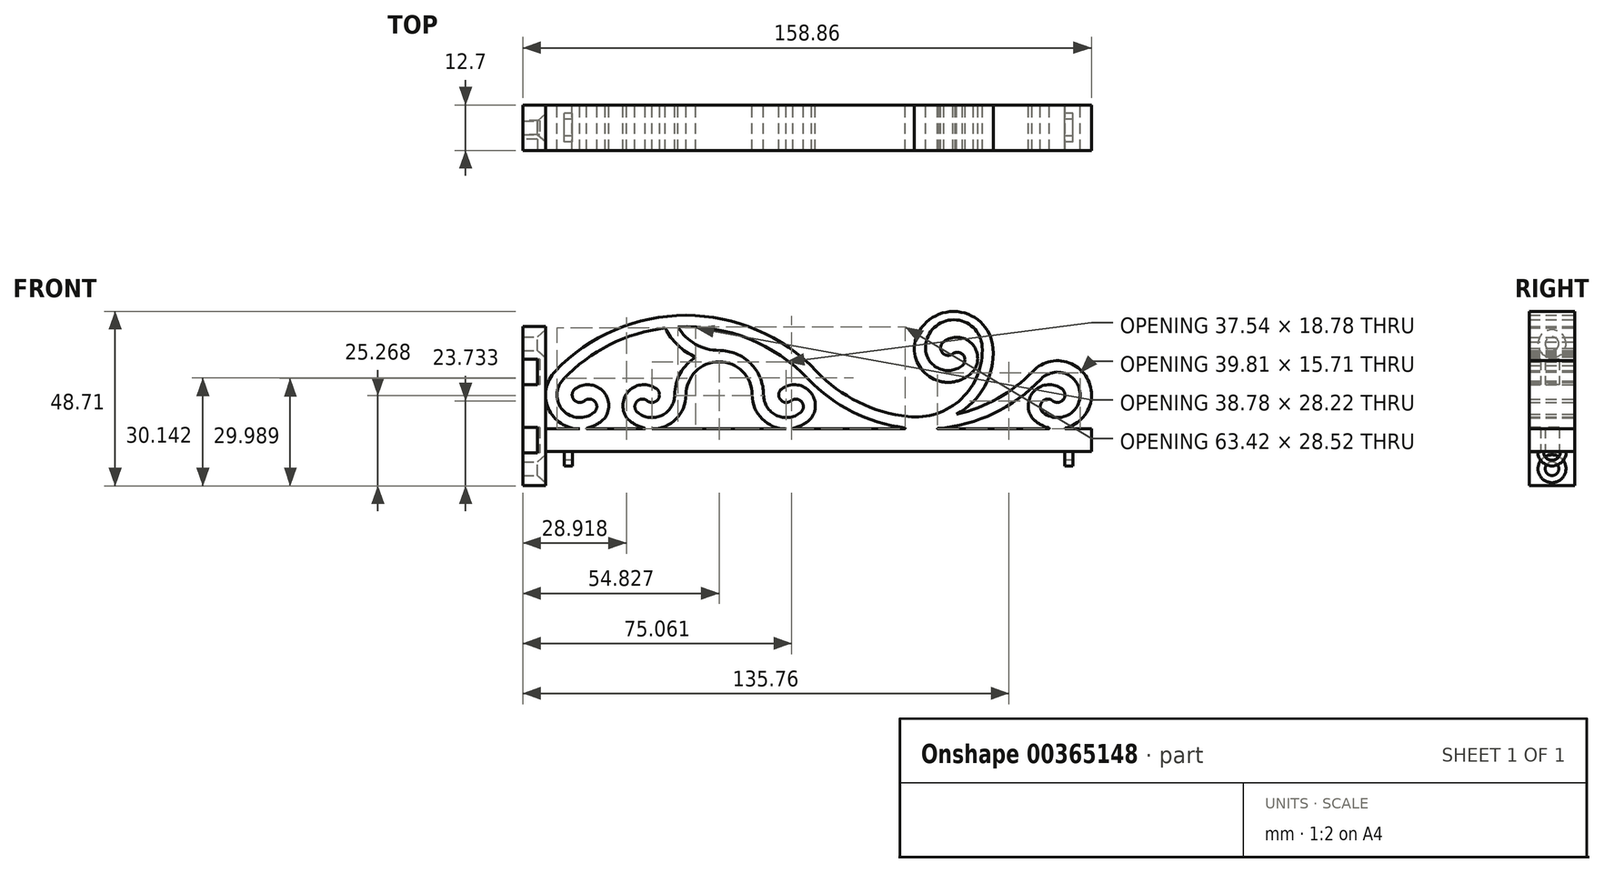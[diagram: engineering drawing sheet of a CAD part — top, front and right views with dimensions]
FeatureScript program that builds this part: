
annotation { "Feature Type Name" : "Feature", "Feature Type Description" : "" }
export const myFeature = defineFeature(function(context is Context, id is Id, definition is map)
    precondition{}
    {
        {
            var Q0;
            Q0=qCreatedBy(makeId("Front.planeOp"),FACE);
            var sketch = newSketch(context, id + "F0", { "sketchPlane" : qUnion([Q0])});
            skLineSegment(sketch, "E0.bottom", {"start": v(-3.17, 22.23) * mm, "end": v(3.18, 22.23) * mm, "construction": true});
            skLineSegment(sketch, "E0.top", {"start": v(-3.17, -22.23) * mm, "end": v(3.18, -22.23) * mm, "construction": true});
            skLineSegment(sketch, "E0.right", {"start": v(3.18, 22.23) * mm, "end": v(3.18, -22.23) * mm});
            skPoint(sketch, "E0.middle", {"position": v(0, 0) * mm});
            skLineSegment(sketch, "E1", {"start": v(3.18, 22.23) * mm, "end": v(-3.17, 22.23) * mm});
            skLineSegment(sketch, "E2", {"start": v(3.18, -22.23) * mm, "end": v(-3.17, -22.23) * mm});
            skLineSegment(sketch, "E3", {"start": v(-3.17, 22.23) * mm, "end": v(-3.17, -22.23) * mm});
            skSolve(sketch);
        }
        {
            var Q0;
            Q0=makeQuery(id+"F0.imprint","IMPRINT",FACE,{"disambiguationData":[TD([[makeQuery(id+"F0.imprint","IMPRINT",EDGE,{"derivedFrom":sQuery(id+"F0.wireOp",EDGE,"E0.right")}),-1.0]])]});
            extrude(context, id + "F1", {"entities" : qUnion([Q0]), "endBound" : BoundingType.SYMMETRIC, "depth" : 12.7 * mm});
        }
        {
            var Q0;
            Q0=makeQuery(id+"F1.opExtrude","SWEPT_FACE",FACE,{"disambiguationData":[OSD([sQuery(id+"F0.wireOp",EDGE,"E3")])]});
            var sketch = newSketch(context, id + "F2", { "sketchPlane" : qUnion([Q0])});
            skLineSegment(sketch, "E4", {"start": v(0, 9.53) * mm, "end": v(0, -9.53) * mm, "construction": true});
            skLineSegment(sketch, "E5.bottom", {"start": v(-1.97, 13.08) * mm, "end": v(1.97, 13.08) * mm});
            skLineSegment(sketch, "E5.top", {"start": v(-1.97, 5.97) * mm, "end": v(1.97, 5.97) * mm});
            skLineSegment(sketch, "E5.left", {"start": v(-1.97, 13.08) * mm, "end": v(-1.97, 5.97) * mm});
            skLineSegment(sketch, "E5.right", {"start": v(1.97, 13.08) * mm, "end": v(1.97, 5.97) * mm});
            skPoint(sketch, "E5.middle", {"position": v(0, 9.53) * mm});
            skLineSegment(sketch, "E6.bottom", {"start": v(-1.97, -5.97) * mm, "end": v(1.97, -5.97) * mm});
            skLineSegment(sketch, "E6.top", {"start": v(-1.97, -13.08) * mm, "end": v(1.97, -13.08) * mm});
            skLineSegment(sketch, "E6.left", {"start": v(-1.97, -5.97) * mm, "end": v(-1.97, -13.08) * mm});
            skLineSegment(sketch, "E6.right", {"start": v(1.97, -5.97) * mm, "end": v(1.97, -13.08) * mm});
            skPoint(sketch, "E6.middle", {"position": v(0, -9.53) * mm});
            skSolve(sketch);
        }
        {
            var Q0;
            Q0=makeQuery(id+"F2.imprint","IMPRINT",FACE,{"disambiguationData":[TD([[makeQuery(id+"F2.imprint","IMPRINT",EDGE,{"derivedFrom":sQuery(id+"F2.wireOp",EDGE,"E5.bottom")}),-1.0]])]});
            var Q1;
            Q1=makeQuery(id+"F2.imprint","IMPRINT",FACE,{"disambiguationData":[TD([[makeQuery(id+"F2.imprint","IMPRINT",EDGE,{"derivedFrom":sQuery(id+"F2.wireOp",EDGE,"E6.bottom")}),-1.0]])]});
            extrude(context, id + "F3", {"entities" : qUnion([Q0, Q1]), "operationType" : NewBodyOperationType.REMOVE, "oppositeDirection" : true, "depth" : 4.76 * mm});
        }
        {
            var Q0;
            Q0=makeQuery(id+"F1.opExtrude","SWEPT_FACE",FACE,{"disambiguationData":[OSD([sQuery(id+"F0.wireOp",EDGE,"E0.right")])]});
            var sketch = newSketch(context, id + "F4", { "sketchPlane" : qUnion([Q0])});
            skLineSegment(sketch, "E7", {"start": v(0, 17.46) * mm, "end": v(0, -17.46) * mm, "construction": true});
            skPoint(sketch, "E8", {"position": v(0, 17.46) * mm});
            skPoint(sketch, "E9", {"position": v(0, -17.46) * mm});
            skSolve(sketch);
        }
        {
            var Q0;
            Q0=sQuery(id+"F4.wireOp",VERTEX,"E8");
            var Q1;
            Q1=sQuery(id+"F4.wireOp",VERTEX,"E9");
            var Q2;
            Q2=makeQuery(id+"F1.opExtrude","SWEPT_BODY",BODY,{"disambiguationData":[OSD([sQuery(id+"F0.wireOp",EDGE,"E0.right"),sQuery(id+"F0.wireOp",EDGE,"E1"),sQuery(id+"F0.wireOp",EDGE,"E2"),sQuery(id+"F0.wireOp",EDGE,"E3")])]});
            hole(context, id + "F5", {"style" : HoleStyle.C_SINK, "endStyle" : HoleEndStyle.THROUGH, "standardTappedOrClearance" : lookupTablePath({ "standard" : "ANSI", "fit" : "Normal (ASME)", "size" : "#6", "type" : "Clearance" }), "standardBlindInLast" : lookupTablePath({ "fit" : "Free", "standard" : "ANSI", "size" : "#6", "type" : "Clearance" }), "holeDiameter" : 3.8 * mm, "cSinkDiameter" : 7.8 * mm, "cSinkAngle" : 82 * degree, "isTappedThrough" : true, "tappedDepth" : 12.7 * mm, "tapClearance" : 3, "locations" : qUnion([Q0, Q1]), "scope" : qUnion([Q2])});
        }
        {
            var Q0;
            Q0=makeQuery(id+"F1.opExtrude","SWEPT_FACE",FACE,{"disambiguationData":[OSD([sQuery(id+"F0.wireOp",EDGE,"E0.right")])]});
            var sketch = newSketch(context, id + "F6", { "sketchPlane" : qUnion([Q0])});
            skLineSegment(sketch, "E10.bottom", {"start": v(-6.35, 12.7) * mm, "end": v(6.35, 12.7) * mm});
            skLineSegment(sketch, "E10.top", {"start": v(-6.35, -12.7) * mm, "end": v(6.35, -12.7) * mm});
            skLineSegment(sketch, "E10.left", {"start": v(-6.35, 12.7) * mm, "end": v(-6.35, -12.7) * mm});
            skLineSegment(sketch, "E10.right", {"start": v(6.35, 12.7) * mm, "end": v(6.35, -12.7) * mm});
            skPoint(sketch, "E10.middle", {"position": v(0, 0) * mm});
            skSolve(sketch);
        }
        {
            var Q0;
            Q0=qCreatedBy(makeId("Front.planeOp"),FACE);
            var sketch = newSketch(context, id + "F7", { "sketchPlane" : qUnion([Q0])});
            skLineSegment(sketch, "E11.bottom", {"start": v(3.18, -6.35) * mm, "end": v(12.7, -6.35) * mm});
            skLineSegment(sketch, "E11.top", {"start": v(3.18, -12.7) * mm, "end": v(14.29, -12.7) * mm});
            skLineSegment(sketch, "E11.left", {"start": v(3.18, -6.35) * mm, "end": v(3.18, -12.7) * mm});
            skLineSegment(sketch, "E11.right", {"start": v(155.68, -6.35) * mm, "end": v(155.68, -12.7) * mm});
            skLineSegment(sketch, "E12", {"start": v(0, 0) * mm, "end": v(3.22, 0) * mm, "construction": true});
            skArc(sketch, "E13", {"start": v(5.8, 9.75) * mm, "mid": v(3.94, -0.57) * mm, "end": v(12.7, -6.35) * mm});
            skArc(sketch, "E14", {"start": v(8.1, 7.56) * mm, "mid": v(8.03, -1.13) * mm, "end": v(16.69, -1.77) * mm});
            skArc(sketch, "E15", {"start": v(11.44, 4.87) * mm, "mid": v(11.03, 1.88) * mm, "end": v(14.03, 1.53) * mm});
            skArc(sketch, "E16", {"start": v(16.69, -1.77) * mm, "mid": v(17, 1.21) * mm, "end": v(14.03, 1.53) * mm});
            skArc(sketch, "E17", {"start": v(19.77, -3.21) * mm, "mid": v(19.04, 4.36) * mm, "end": v(11.44, 4.87) * mm});
            skArc(sketch, "E18", {"start": v(78.9, 9.75) * mm, "mid": v(42.36, 25.4) * mm, "end": v(5.8, 9.75) * mm});
            skArc(sketch, "E19", {"start": v(76.6, 7.56) * mm, "mid": v(59.98, 18.82) * mm, "end": v(40.17, 22.17) * mm});
            skLineSegment(sketch, "E20", {"start": v(42.36, 25.4) * mm, "end": v(79.43, 25.4) * mm, "construction": true});
            skLineSegment(sketch, "E21", {"start": v(79.43, -6.35) * mm, "end": v(79.43, 38.2) * mm, "construction": true});
            skArc(sketch, "E22.MirrorCS", {"start": v(141.55, 7.56) * mm, "mid": v(152.49, 3.59) * mm, "end": v(142.16, -1.77) * mm});
            skArc(sketch, "E23.MirrorC", {"start": v(139.26, 9.75) * mm, "mid": v(154.38, 7.97) * mm, "end": v(148.47, -6.06) * mm});
            skArc(sketch, "E24.MirrorCS", {"start": v(147.4, 4.87) * mm, "mid": v(147.82, 1.88) * mm, "end": v(144.82, 1.53) * mm});
            skArc(sketch, "E25.MirrorCS", {"start": v(142.16, -1.77) * mm, "mid": v(141.84, 1.21) * mm, "end": v(144.82, 1.53) * mm});
            skArc(sketch, "E26.MirrorCS", {"start": v(139.08, -3.21) * mm, "mid": v(139.81, 4.36) * mm, "end": v(147.4, 4.87) * mm});
            skArc(sketch, "E27", {"start": v(78.9, 9.75) * mm, "mid": v(90.56, 1.17) * mm, "end": v(104.44, -2.92) * mm});
            skArc(sketch, "E28", {"start": v(76.6, 7.56) * mm, "mid": v(88.85, -1.53) * mm, "end": v(103.44, -6) * mm});
            skPoint(sketch, "E29.orphan", {"position": v(18.91, 4.48) * mm});
            skPoint(sketch, "E30.orphan", {"position": v(139.94, 4.48) * mm});
            skArc(sketch, "E31", {"start": v(103.41, -6.35) * mm, "mid": v(103.6, -6.18) * mm, "end": v(103.44, -6) * mm});
            skArc(sketch, "E32", {"start": v(112.74, -6.2) * mm, "mid": v(112.67, -6.28) * mm, "end": v(112.75, -6.35) * mm});
            skArc(sketch, "E33.trimOffspring", {"start": v(112.74, -6.2) * mm, "mid": v(128.41, -1.97) * mm, "end": v(141.55, 7.56) * mm});
            skLineSegment(sketch, "E34.trimOffspring", {"start": v(112.75, -6.35) * mm, "end": v(143.75, -6.35) * mm});
            skArc(sketch, "E35", {"start": v(148.47, -6.06) * mm, "mid": v(148.36, -6.22) * mm, "end": v(148.5, -6.35) * mm});
            skArc(sketch, "E36", {"start": v(143.75, -6.35) * mm, "mid": v(143.9, -6.22) * mm, "end": v(143.8, -6.05) * mm});
            skArc(sketch, "E37.trimOffspring", {"start": v(143.8, -6.05) * mm, "mid": v(141.23, -4.98) * mm, "end": v(139.08, -3.21) * mm});
            skLineSegment(sketch, "E38.trimOffspring", {"start": v(148.5, -6.35) * mm, "end": v(155.68, -6.35) * mm});
            skLineSegment(sketch, "E39", {"start": v(12.7, -6.35) * mm, "end": v(12.7, -6.35) * mm});
            skArc(sketch, "E40", {"start": v(14.67, -6.14) * mm, "mid": v(14.58, -6.26) * mm, "end": v(14.69, -6.35) * mm});
            skArc(sketch, "E41.trimOffspring", {"start": v(14.67, -6.14) * mm, "mid": v(17.45, -5.08) * mm, "end": v(19.77, -3.21) * mm});
            skLineSegment(sketch, "E42.trimOffspring", {"start": v(14.69, -6.35) * mm, "end": v(70.42, -6.35) * mm});
            skLineSegment(sketch, "E43", {"start": v(42.36, 25.4) * mm, "end": v(3.22, 25.4) * mm, "construction": true});
            skLineSegment(sketch, "E44", {"start": v(22.79, 25.4) * mm, "end": v(22.79, -6.35) * mm, "construction": true});
            skArc(sketch, "E45.MirrorCS", {"start": v(28.9, -1.77) * mm, "mid": v(28.57, 1.21) * mm, "end": v(31.55, 1.53) * mm});
            skLineSegment(sketch, "E46.MirrorCS", {"start": v(32.88, -6.35) * mm, "end": v(32.88, -6.35) * mm});
            skPoint(sketch, "E47.MirrorP", {"position": v(26.66, 4.48) * mm});
            skArc(sketch, "E48.MirrorCS", {"start": v(30.91, -6.14) * mm, "mid": v(31, -6.26) * mm, "end": v(30.9, -6.35) * mm});
            skLineSegment(sketch, "E49.MirrorCS", {"start": v(42.4, -6.35) * mm, "end": v(32.88, -6.35) * mm});
            skLineSegment(sketch, "E50.MirrorCS", {"start": v(45.58, 0) * mm, "end": v(42.36, 0) * mm, "construction": true});
            skArc(sketch, "E51.MirrorCS", {"start": v(39.23, 3.18) * mm, "mid": v(35.62, -2.55) * mm, "end": v(28.9, -1.77) * mm});
            skArc(sketch, "E52.MirrorCS", {"start": v(30.91, -6.14) * mm, "mid": v(28.13, -5.08) * mm, "end": v(25.81, -3.21) * mm});
            skArc(sketch, "E53.MirrorCS", {"start": v(34.13, 4.87) * mm, "mid": v(34.55, 1.88) * mm, "end": v(31.55, 1.53) * mm});
            skArc(sketch, "E54.MirrorCS", {"start": v(25.81, -3.21) * mm, "mid": v(26.54, 4.36) * mm, "end": v(34.13, 4.87) * mm});
            skLineSegment(sketch, "E55", {"start": v(42.36, 25.4) * mm, "end": v(42.4, -6.35) * mm, "construction": true});
            skLineSegment(sketch, "E56", {"start": v(60.9, 25.4) * mm, "end": v(60.9, -6.35) * mm, "construction": true});
            skLineSegment(sketch, "E57", {"start": v(60.9, 25.4) * mm, "end": v(42.4, -6.35) * mm, "construction": true});
            skLineSegment(sketch, "E58", {"start": v(51.65, 9.53) * mm, "end": v(51.65, 17.18) * mm, "construction": true});
            skArc(sketch, "E59.MirrorCS", {"start": v(64.07, 3.18) * mm, "mid": v(67.68, -2.55) * mm, "end": v(74.4, -1.77) * mm});
            skArc(sketch, "E60.MirrorCS", {"start": v(74.4, -1.77) * mm, "mid": v(74.72, 1.21) * mm, "end": v(71.74, 1.53) * mm});
            skArc(sketch, "E61.MirrorCS", {"start": v(72.38, -6.14) * mm, "mid": v(75.16, -5.08) * mm, "end": v(77.48, -3.21) * mm});
            skLineSegment(sketch, "E62.MirrorCS", {"start": v(70.42, -6.35) * mm, "end": v(70.42, -6.35) * mm});
            skPoint(sketch, "E63.MirrorP", {"position": v(76.63, 4.48) * mm});
            skArc(sketch, "E64.MirrorCS", {"start": v(69.16, 4.87) * mm, "mid": v(68.74, 1.88) * mm, "end": v(71.74, 1.53) * mm});
            skArc(sketch, "E65.MirrorCS", {"start": v(72.38, -6.14) * mm, "mid": v(72.3, -6.26) * mm, "end": v(72.4, -6.35) * mm});
            skArc(sketch, "E66.MirrorCS", {"start": v(77.48, -3.21) * mm, "mid": v(76.75, 4.36) * mm, "end": v(69.16, 4.87) * mm});
            skLineSegment(sketch, "E67.MirrorCS", {"start": v(60.9, -6.35) * mm, "end": v(70.42, -6.35) * mm});
            skArc(sketch, "E68", {"start": v(60.9, 3.18) * mm, "mid": v(51.64, 12.43) * mm, "end": v(42.39, 3.18) * mm});
            skArc(sketch, "E69", {"start": v(64.07, 3.18) * mm, "mid": v(60.42, 11.97) * mm, "end": v(51.62, 15.6) * mm});
            skLineSegment(sketch, "E70", {"start": v(51.65, 9.53) * mm, "end": v(26.5, 9.75) * mm, "construction": true});
            skArc(sketch, "E71", {"start": v(40.17, 22.17) * mm, "mid": v(45.01, 17.35) * mm, "end": v(51.62, 15.6) * mm});
            skArc(sketch, "E72", {"start": v(36.56, 21.87) * mm, "mid": v(40.1, 17.03) * mm, "end": v(45.13, 13.74) * mm});
            skArc(sketch, "E73.trimOffspring", {"start": v(36.56, 21.87) * mm, "mid": v(21.1, 17.18) * mm, "end": v(8.1, 7.56) * mm});
            skArc(sketch, "E74.trimOffspring", {"start": v(45.13, 13.74) * mm, "mid": v(40.8, 9.23) * mm, "end": v(39.23, 3.18) * mm});
            skPoint(sketch, "E75.orphan", {"position": v(51.64, 12.43) * mm});
            skArc(sketch, "E76.trimOffspring", {"start": v(42.39, 3.18) * mm, "mid": v(39.6, -3.56) * mm, "end": v(32.88, -6.35) * mm});
            skPoint(sketch, "E77.orphan", {"position": v(37.47, 7.56) * mm});
            skPoint(sketch, "E78.MirrorCS.start.orphan", {"position": v(39.77, 9.75) * mm});
            skArc(sketch, "E79.trimOffspring", {"start": v(60.9, 3.18) * mm, "mid": v(63.68, -3.56) * mm, "end": v(70.42, -6.35) * mm});
            skPoint(sketch, "E80.MirrorCS.start.orphan", {"position": v(63.52, 9.75) * mm});
            skPoint(sketch, "E81.orphan", {"position": v(65.82, 7.56) * mm});
            skLineSegment(sketch, "E82.trimOffspring", {"start": v(72.4, -6.35) * mm, "end": v(103.41, -6.35) * mm});
            skArc(sketch, "E83.MirrorCS", {"start": v(109.3, 16.67) * mm, "mid": v(112.74, 10.67) * mm, "end": v(119.62, 11.38) * mm});
            skArc(sketch, "E84.MirrorCS", {"start": v(119.62, 11.38) * mm, "mid": v(119.87, 14.3) * mm, "end": v(116.97, 14.67) * mm});
            skArc(sketch, "E85.MirrorCS", {"start": v(117.61, 6.91) * mm, "mid": v(120.4, 7.98) * mm, "end": v(122.71, 9.85) * mm});
            skPoint(sketch, "E86.MirrorP", {"position": v(121.85, 17.33) * mm});
            skArc(sketch, "E87.MirrorCS", {"start": v(114.38, 18.01) * mm, "mid": v(113.97, 15.02) * mm, "end": v(116.97, 14.67) * mm});
            skArc(sketch, "E88.MirrorCS", {"start": v(122.71, 9.85) * mm, "mid": v(122.14, 17.6) * mm, "end": v(114.38, 18.01) * mm});
            skArc(sketch, "E89.trimOffspring", {"start": v(106.12, 16.23) * mm, "mid": v(108.08, 10.44) * mm, "end": v(113.16, 7.04) * mm});
            skArc(sketch, "E90", {"start": v(113.16, 7.04) * mm, "mid": v(115.38, 6.66) * mm, "end": v(117.61, 6.91) * mm});
            skArc(sketch, "E91", {"start": v(128.16, 16.23) * mm, "mid": v(117.14, 26.48) * mm, "end": v(106.12, 16.23) * mm});
            skArc(sketch, "E92", {"start": v(125.13, 16.67) * mm, "mid": v(117.22, 24.15) * mm, "end": v(109.3, 16.67) * mm});
            skArc(sketch, "E93", {"start": v(104.44, -2.92) * mm, "mid": v(119.33, 2.07) * mm, "end": v(125.13, 16.67) * mm});
            skArc(sketch, "E94", {"start": v(117.96, -2.22) * mm, "mid": v(125.8, 5.49) * mm, "end": v(128.16, 16.23) * mm});
            skArc(sketch, "E95.trimOffspring", {"start": v(117.96, -2.22) * mm, "mid": v(129.5, 2.17) * mm, "end": v(139.26, 9.75) * mm});
            skLineSegment(sketch, "E96.trimOffspring", {"start": v(144.56, -12.7) * mm, "end": v(155.68, -12.7) * mm});
            skLineSegment(sketch, "E97.MirrorCS", {"start": v(14.29, -12.7) * mm, "end": v(14.29, -12.7) * mm});
            skLineSegment(sketch, "E98.trimOffspring", {"start": v(14.29, -12.7) * mm, "end": v(144.56, -12.7) * mm});
            skSolve(sketch);
        }
        {
            var Q0;
            Q0=makeQuery(id+"F7.imprint","IMPRINT",FACE,{"disambiguationData":[TD([[makeQuery(id+"F7.imprint","IMPRINT",EDGE,{"derivedFrom":sQuery(id+"F7.wireOp",EDGE,"E11.bottom")}),-1.0]])]});
            extrude(context, id + "F8", {"entities" : qUnion([Q0]), "endBound" : BoundingType.SYMMETRIC, "depth" : 12.7 * mm});
        }
        {
            var Q0;
            Q0=makeQuery(id+"F8.opExtrude","SWEPT_FACE",FACE,{"disambiguationData":[OSD([sQuery(id+"F7.wireOp",EDGE,"E11.right")])]});
            cPlane(context, id + "F9", {"entities" : qUnion([Q0]), "cplaneType" : CPlaneType.OFFSET, "offset" : 6.35 * mm, "oppositeDirection" : true, "width" : 152.4 * mm, "height" : 152.4 * mm});
        }
        {
            var Q0;
            Q0=qCreatedBy(id+"F9.planeOp",FACE);
            var sketch = newSketch(context, id + "F10", { "sketchPlane" : qUnion([Q0])});
            skArc(sketch, "E99", {"start": v(-3.97, -12.7) * mm, "mid": v(0, -16.67) * mm, "end": v(3.97, -12.7) * mm});
            skLineSegment(sketch, "E100", {"start": v(-3.97, -12.7) * mm, "end": v(-3.97, -10.42) * mm, "construction": true});
            skLineSegment(sketch, "E101", {"start": v(-3.97, -10.42) * mm, "end": v(3.97, -10.42) * mm, "construction": true});
            skLineSegment(sketch, "E102", {"start": v(3.97, -10.42) * mm, "end": v(3.97, -12.7) * mm, "construction": true});
            skArc(sketch, "E103.0", {"start": v(-2.38, -12.7) * mm, "mid": v(0, -15.08) * mm, "end": v(2.38, -12.7) * mm});
            skLineSegment(sketch, "E104", {"start": v(-3.97, -12.7) * mm, "end": v(-2.38, -12.7) * mm});
            skLineSegment(sketch, "E105", {"start": v(2.38, -12.7) * mm, "end": v(3.97, -12.7) * mm});
            skSolve(sketch);
        }
        {
            var Q0;
            Q0=makeQuery(id+"F10.imprint","IMPRINT",FACE,{"disambiguationData":[TD([[makeQuery(id+"F10.imprint","IMPRINT",EDGE,{"derivedFrom":sQuery(id+"F10.wireOp",EDGE,"E99")}),1.0]])]});
            extrude(context, id + "F11", {"entities" : qUnion([Q0]), "operationType" : NewBodyOperationType.ADD, "endBound" : BoundingType.SYMMETRIC, "depth" : 2.3 * mm});
        }
        {
            var Q0;
            {var subQ3=sQuery(id+"F6.wireOp",EDGE,"E10.top");Q0=makeQuery(id+"F6.imprint","IMPRINT",FACE,{"disambiguationData":[TD([[makeQuery(id+"F6.imprint","IMPRINT",EDGE,{"derivedFrom":subQ3}),-1.0]])]});}
            cPlane(context, id + "F12", {"entities" : qUnion([Q0]), "cplaneType" : CPlaneType.OFFSET, "offset" : 6.35 * mm, "width" : 152.4 * mm, "height" : 152.4 * mm});
        }
        {
            var Q0;
            Q0=qCreatedBy(id+"F12.planeOp",FACE);
            var sketch = newSketch(context, id + "F13", { "sketchPlane" : qUnion([Q0])});
            skArc(sketch, "E106.0", {"start": v(-2.38, -12.7) * mm, "mid": v(0, -15.08) * mm, "end": v(2.38, -12.7) * mm});
            skLineSegment(sketch, "E106.1", {"start": v(-3.97, -12.7) * mm, "end": v(-2.38, -12.7) * mm});
            skLineSegment(sketch, "E106.2", {"start": v(2.38, -12.7) * mm, "end": v(3.97, -12.7) * mm});
            skArc(sketch, "E106.3", {"start": v(-3.97, -12.7) * mm, "mid": v(0, -16.67) * mm, "end": v(3.97, -12.7) * mm});
            skSolve(sketch);
        }
        {
            var Q0;
            Q0 = qSketchRegion(id + "F13", true);
            extrude(context, id + "F14", {"entities" : qUnion([Q0]), "operationType" : NewBodyOperationType.ADD, "endBound" : BoundingType.SYMMETRIC, "depth" : 2.3 * mm});
        }
        {
            var Q0;
            Q0=makeQuery(id+"F1.opExtrude","CAP_FACE",FACE,{"disambiguationData":[OSD([sQuery(id+"F0.wireOp",EDGE,"E0.right"),sQuery(id+"F0.wireOp",EDGE,"E1"),sQuery(id+"F0.wireOp",EDGE,"E2"),sQuery(id+"F0.wireOp",EDGE,"E3")])],"isStart":false});
            var sketch = newSketch(context, id + "F15", { "sketchPlane" : qUnion([Q0])});
            skLineSegment(sketch, "E107.0", {"start": v(-3.17, 13.08) * mm, "end": v(-3.17, 5.97) * mm});
            skLineSegment(sketch, "E108", {"start": v(-3.17, 13.08) * mm, "end": v(0.89, 13.08) * mm});
            skLineSegment(sketch, "E109", {"start": v(0.89, 13.08) * mm, "end": v(0.89, 5.97) * mm});
            skLineSegment(sketch, "E110", {"start": v(0.89, 5.97) * mm, "end": v(-3.17, 5.97) * mm});
            skLineSegment(sketch, "E111", {"start": v(-1.03, 0) * mm, "end": v(-6.23, 0) * mm, "construction": true});
            skLineSegment(sketch, "E112.MirrorCS", {"start": v(-3.17, -13.08) * mm, "end": v(-3.17, -5.97) * mm});
            skLineSegment(sketch, "E113.MirrorCS", {"start": v(0.89, -5.97) * mm, "end": v(-3.17, -5.97) * mm});
            skLineSegment(sketch, "E114.MirrorCS", {"start": v(0.89, -13.08) * mm, "end": v(0.89, -5.97) * mm});
            skLineSegment(sketch, "E115.MirrorCS", {"start": v(-3.17, -13.08) * mm, "end": v(0.89, -13.08) * mm});
            skSolve(sketch);
        }
        {
            var Q0;
            Q0 = qSketchRegion(id + "F15", true);
            extrude(context, id + "F16", {"entities" : qUnion([Q0]), "operationType" : NewBodyOperationType.REMOVE, "oppositeDirection" : true, "depth" : 3.17 * mm, "offsetDistance" : 25.4 * mm});
        }
    });
